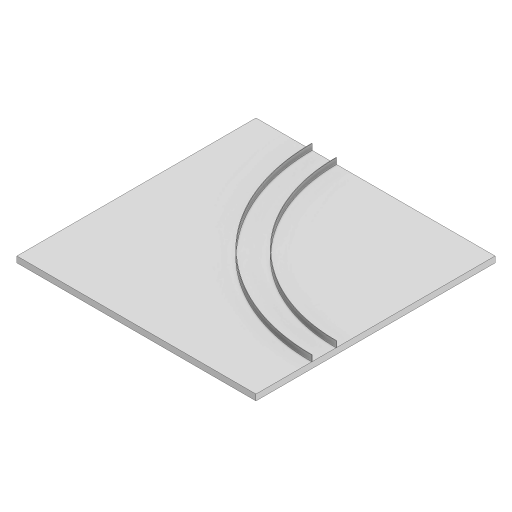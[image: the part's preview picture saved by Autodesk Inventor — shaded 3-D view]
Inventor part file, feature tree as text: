
AUTODESK INVENTOR PART (.ipt)
format: ipt  version: 2023 (Build 270158000, 158)  size: 120,832 bytes
history: native  units: in
note: dims shown in document units (in); Inventor stores cm internally (conversion verified against a paired STEP export)
features: extrude x2, sketch x2
ambient origin geometry x8: Origin, YZ Plane, XZ Plane, XY Plane, X Axis, Y Axis, Z Axis, Center Point
bodies: Solid1 (feature_tree)
feature tree (4):
  extrude  "Extrusion1"  Depth=3937.0079in
  extrude  "Extrusion2"  Depth=98.4252in
  sketch  "Sketch1"  dims[d0=3937.0079in d1=3937.0079in]
  sketch  "Sketch2"  dims[d2=98.4252in d3=0.0in d5=8.0in d6=8.0in d7=393.7008in d8=98.4252in d9=0.0in]
